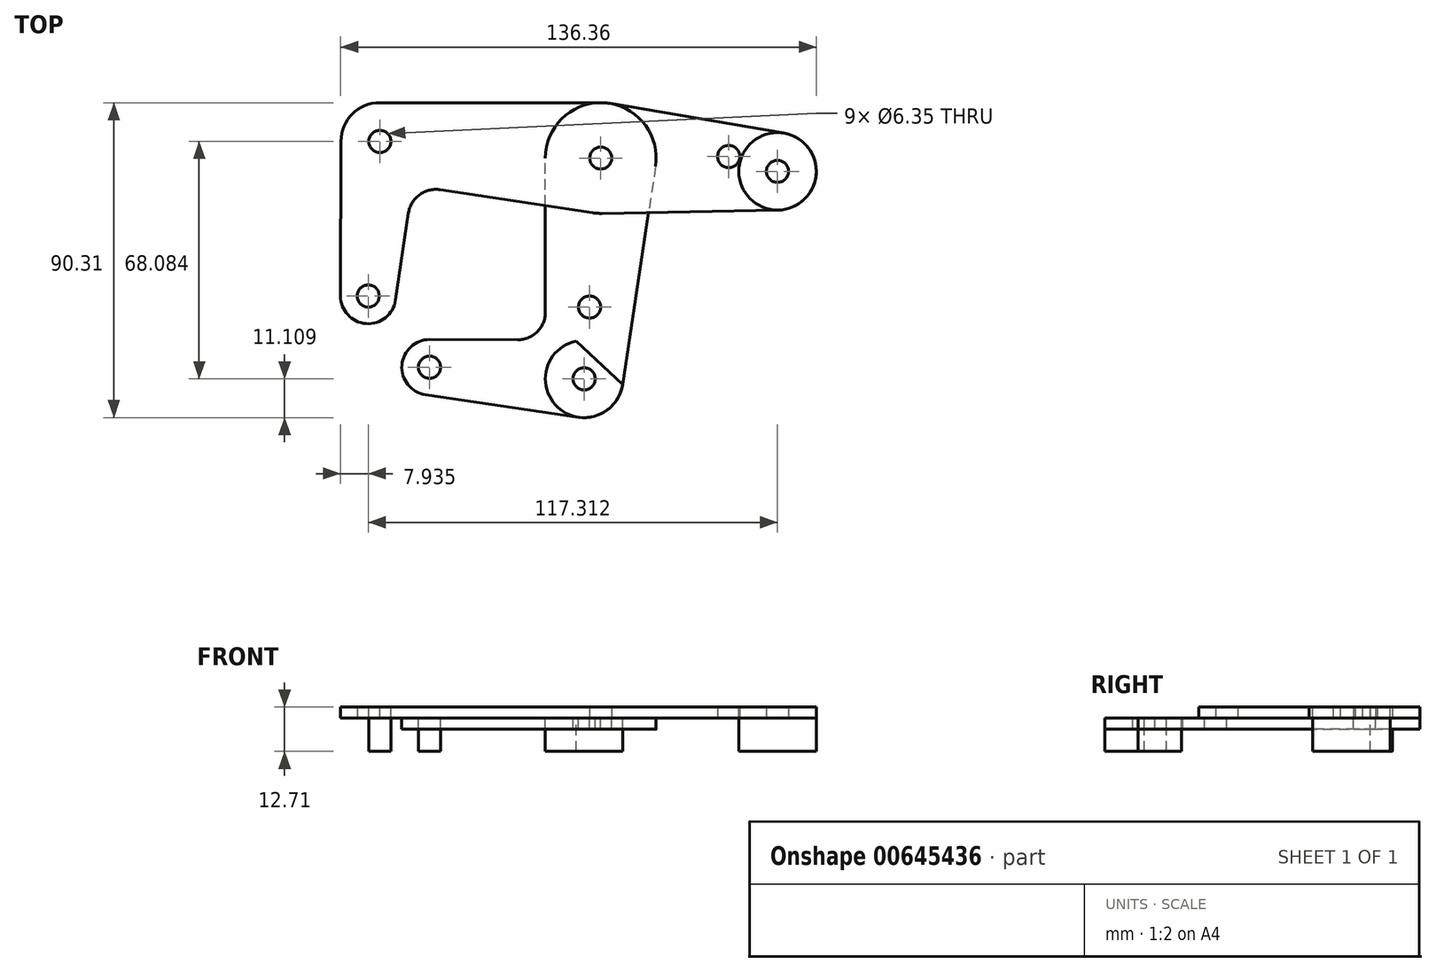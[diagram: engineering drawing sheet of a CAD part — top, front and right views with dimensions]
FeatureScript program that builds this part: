
annotation { "Feature Type Name" : "Feature", "Feature Type Description" : "" }
export const myFeature = defineFeature(function(context is Context, id is Id, definition is map)
    precondition{}
    {
        {
            var Q0;
            Q0=qCreatedBy(makeId("Top.planeOp"),FACE);
            var sketch = newSketch(context, id + "F0", { "sketchPlane" : qUnion([Q0])});
            skCircle(sketch, "E0", {"center": v(0, 0) * mm, "radius": 15.88 * mm});
            skLineSegment(sketch, "E1", {"start": v(0, 0) * mm, "end": v(-63.32, 4.76) * mm, "construction": true});
            skLineSegment(sketch, "E2", {"start": v(0, 0) * mm, "end": v(50.66, -3.8) * mm, "construction": true});
            skLineSegment(sketch, "E3", {"start": v(-63.32, 4.76) * mm, "end": v(-66.65, -39.56) * mm, "construction": true});
            skCircle(sketch, "E4", {"center": v(-63.32, 4.76) * mm, "radius": 11.11 * mm});
            skCircle(sketch, "E5", {"center": v(-66.65, -39.56) * mm, "radius": 7.94 * mm});
            skCircle(sketch, "E6", {"center": v(50.66, -3.8) * mm, "radius": 11.11 * mm});
            skCircle(sketch, "E7", {"center": v(36.66, 0.43) * mm, "radius": 3.18 * mm});
            skLineSegment(sketch, "E8", {"start": v(36.66, 0.43) * mm, "end": v(36.42, -2.74) * mm});
            skLineSegment(sketch, "E9", {"start": v(2.67, 15.65) * mm, "end": v(52.53, 7.14) * mm});
            skLineSegment(sketch, "E10", {"start": v(50.87, -14.92) * mm, "end": v(0.3, -15.87) * mm});
            skLineSegment(sketch, "E11", {"start": v(0, 0) * mm, "end": v(-4.76, -63.32) * mm, "construction": true});
            skLineSegment(sketch, "E12", {"start": v(-4.76, -63.32) * mm, "end": v(-49.09, -59.99) * mm, "construction": true});
            skCircle(sketch, "E13", {"center": v(-4.76, -63.32) * mm, "radius": 11.11 * mm});
            skLineSegment(sketch, "E14", {"start": v(-58.8, -40.72) * mm, "end": v(-55.12, -15.79) * mm});
            skLineSegment(sketch, "E15", {"start": v(-2.37, -15.7) * mm, "end": v(-46.07, -9.09) * mm});
            skArc(sketch, "E16.filletArc", {"start": v(-46.07, -9.09) * mm, "mid": v(-51.99, -10.56) * mm, "end": v(-55.12, -15.79) * mm});
            skCircle(sketch, "E17", {"center": v(-49.09, -59.99) * mm, "radius": 7.94 * mm});
            skCircle(sketch, "E18", {"center": v(-3.21, -42.73) * mm, "radius": 3.18 * mm});
            skLineSegment(sketch, "E19", {"start": v(-74.6, -39.53) * mm, "end": v(-74.43, 4.8) * mm});
            skLineSegment(sketch, "E20", {"start": v(-63.32, 15.87) * mm, "end": v(0, 15.87) * mm});
            skLineSegment(sketch, "E21", {"start": v(-15.88, -44.2) * mm, "end": v(-15.88, 0) * mm});
            skLineSegment(sketch, "E22", {"start": v(15.7, -2.37) * mm, "end": v(6.22, -64.98) * mm});
            skLineSegment(sketch, "E23", {"start": v(-6.39, -74.31) * mm, "end": v(-50.25, -67.84) * mm});
            skLineSegment(sketch, "E24", {"start": v(-23.85, -52.14) * mm, "end": v(-49.06, -52.05) * mm});
            skCircle(sketch, "E25", {"center": v(50.66, -3.8) * mm, "radius": 3.18 * mm});
            skCircle(sketch, "E26", {"center": v(0, 0) * mm, "radius": 3.18 * mm});
            skCircle(sketch, "E27", {"center": v(-63.32, 4.76) * mm, "radius": 3.18 * mm});
            skCircle(sketch, "E28", {"center": v(-66.65, -39.56) * mm, "radius": 3.18 * mm});
            skCircle(sketch, "E29", {"center": v(-49.09, -59.99) * mm, "radius": 3.18 * mm});
            skCircle(sketch, "E30", {"center": v(-4.76, -63.32) * mm, "radius": 3.18 * mm});
            skArc(sketch, "E31.filletArc", {"start": v(-23.85, -52.14) * mm, "mid": v(-18.21, -49.82) * mm, "end": v(-15.88, -44.2) * mm});
            skLineSegment(sketch, "E32", {"start": v(-66.65, -39.56) * mm, "end": v(-49.09, -59.99) * mm, "construction": true});
            skSolve(sketch);
        }
        {
            var Q0;
            {var subQ0=sQuery(id+"F0.wireOp",EDGE,"E14");Q0=makeQuery(id+"F0.imprint","IMPRINT",FACE,{"disambiguationData":[TD([[makeQuery(id+"F0.imprint","IMPRINT",EDGE,{"derivedFrom":subQ0}),1.0]])]});}
            var Q1;
            Q1=makeQuery(id+"F0.imprint","IMPRINT",FACE,{"disambiguationData":[TD([[makeQuery(id+"F0.imprint","IMPRINT",EDGE,{"derivedFrom":sQuery(id+"F0.wireOp",EDGE,"E27")}),-1.0]])]});
            var Q2;
            Q2=makeQuery(id+"F0.imprint","IMPRINT",FACE,{"disambiguationData":[TD([[makeQuery(id+"F0.imprint","IMPRINT",EDGE,{"derivedFrom":sQuery(id+"F0.wireOp",EDGE,"E26")}),-1.0]])]});
            var Q3;
            Q3=makeQuery(id+"F0.imprint","IMPRINT",FACE,{"disambiguationData":[TD([[makeQuery(id+"F0.imprint","IMPRINT",EDGE,{"derivedFrom":sQuery(id+"F0.wireOp",EDGE,"E25")}),-1.0]])]});
            var Q4;
            Q4=makeQuery(id+"F0.imprint","IMPRINT",FACE,{"disambiguationData":[TD([[makeQuery(id+"F0.imprint","IMPRINT",EDGE,{"derivedFrom":sQuery(id+"F0.wireOp",EDGE,"E7")}),-1.0]])]});
            var Q5;
            {var subQ0=sQuery(id+"F0.wireOp",EDGE,"E10");var subQ1=sQuery(id+"F0.wireOp",EDGE,"E0");var subQ2=makeQuery(id+"F0.imprint","INTERSECT",VERTEX,{"derivedFrom":[subQ1,subQ0]});Q5=makeQuery(id+"F0.imprint","IMPRINT",FACE,{"disambiguationData":[TD([[makeQuery(id+"F0.imprint","IMPRINT",EDGE,{"disambiguationData":[TD([[subQ2,-1.0]])],"derivedFrom":subQ1}),-1.0]])]});}
            var Q6;
            {var subQ0=sQuery(id+"F0.wireOp",EDGE,"E15");var subQ1=sQuery(id+"F0.wireOp",EDGE,"E0");var subQ2=makeQuery(id+"F0.imprint","INTERSECT",VERTEX,{"derivedFrom":[subQ1,subQ0]});Q6=makeQuery(id+"F0.imprint","IMPRINT",FACE,{"disambiguationData":[TD([[makeQuery(id+"F0.imprint","IMPRINT",EDGE,{"disambiguationData":[TD([[subQ2,1.0]])],"derivedFrom":subQ1}),-1.0]])]});}
            var Q7;
            Q7=makeQuery(id+"F0.imprint","IMPRINT",FACE,{"disambiguationData":[TD([[makeQuery(id+"F0.imprint","IMPRINT",EDGE,{"derivedFrom":sQuery(id+"F0.wireOp",EDGE,"E28")}),-1.0]])]});
            extrude(context, id + "F1", {"entities" : qUnion([Q0, Q1, Q2, Q3, Q4, Q5, Q6, Q7]), "depth" : 3.17 * mm, "offsetDistance" : 25.4 * mm});
        }
        {
            var Q0;
            Q0=makeQuery(id+"F0.imprint","IMPRINT",FACE,{"disambiguationData":[TD([[makeQuery(id+"F0.imprint","IMPRINT",EDGE,{"derivedFrom":sQuery(id+"F0.wireOp",EDGE,"E18")}),-1.0]])]});
            var Q1;
            Q1=makeQuery(id+"F0.imprint","IMPRINT",FACE,{"disambiguationData":[TD([[makeQuery(id+"F0.imprint","IMPRINT",EDGE,{"derivedFrom":sQuery(id+"F0.wireOp",EDGE,"E29")}),-1.0]])]});
            var Q2;
            Q2=makeQuery(id+"F0.imprint","IMPRINT",FACE,{"disambiguationData":[TD([[makeQuery(id+"F0.imprint","IMPRINT",EDGE,{"derivedFrom":sQuery(id+"F0.wireOp",EDGE,"E30")}),-1.0]])]});
            var Q3;
            Q3=makeQuery(id+"F0.imprint","IMPRINT",FACE,{"disambiguationData":[TD([[makeQuery(id+"F0.imprint","IMPRINT",EDGE,{"derivedFrom":sQuery(id+"F0.wireOp",EDGE,"E26")}),-1.0]])]});
            var Q4;
            {var subQ0=sQuery(id+"F0.wireOp",EDGE,"E10");var subQ1=sQuery(id+"F0.wireOp",EDGE,"E0");var subQ2=makeQuery(id+"F0.imprint","INTERSECT",VERTEX,{"derivedFrom":[subQ1,subQ0]});Q4=makeQuery(id+"F0.imprint","IMPRINT",FACE,{"disambiguationData":[TD([[makeQuery(id+"F0.imprint","IMPRINT",EDGE,{"disambiguationData":[TD([[subQ2,-1.0]])],"derivedFrom":subQ1}),-1.0]])]});}
            var Q5;
            {var subQ0=sQuery(id+"F0.wireOp",EDGE,"E15");var subQ1=sQuery(id+"F0.wireOp",EDGE,"E0");var subQ2=makeQuery(id+"F0.imprint","INTERSECT",VERTEX,{"derivedFrom":[subQ1,subQ0]});Q5=makeQuery(id+"F0.imprint","IMPRINT",FACE,{"disambiguationData":[TD([[makeQuery(id+"F0.imprint","IMPRINT",EDGE,{"disambiguationData":[TD([[subQ2,1.0]])],"derivedFrom":subQ1}),-1.0]])]});}
            extrude(context, id + "F2", {"entities" : qUnion([Q0, Q1, Q2, Q3, Q4, Q5]), "oppositeDirection" : true, "depth" : 3.17 * mm, "offsetDistance" : 25.4 * mm});
        }
        {
            var Q0;
            Q0=makeQuery(id+"F1.opExtrude","CAP_FACE",FACE,{"disambiguationData":[OSD([sQuery(id+"F0.wireOp",EDGE,"E0"),sQuery(id+"F0.wireOp",EDGE,"E4"),sQuery(id+"F0.wireOp",EDGE,"E5"),sQuery(id+"F0.wireOp",EDGE,"E6"),sQuery(id+"F0.wireOp",EDGE,"E7"),sQuery(id+"F0.wireOp",EDGE,"E9"),sQuery(id+"F0.wireOp",EDGE,"E10"),sQuery(id+"F0.wireOp",EDGE,"E14"),sQuery(id+"F0.wireOp",EDGE,"E15"),sQuery(id+"F0.wireOp",EDGE,"E16.filletArc"),sQuery(id+"F0.wireOp",EDGE,"E19"),sQuery(id+"F0.wireOp",EDGE,"E20"),sQuery(id+"F0.wireOp",EDGE,"E25"),sQuery(id+"F0.wireOp",EDGE,"E26"),sQuery(id+"F0.wireOp",EDGE,"E27"),sQuery(id+"F0.wireOp",EDGE,"E28")])],"isStart":false});
            var sketch = newSketch(context, id + "F3", { "sketchPlane" : qUnion([Q0])});
            skCircle(sketch, "E33", {"center": v(-63.32, 4.76) * mm, "radius": 3.98 * mm});
            skCircle(sketch, "E34", {"center": v(0, 0) * mm, "radius": 3.98 * mm});
            skCircle(sketch, "E35", {"center": v(50.66, -3.8) * mm, "radius": 11.11 * mm});
            skSolve(sketch);
        }
        {
            var Q0;
            Q0=makeQuery(id+"F2.opExtrude","CAP_FACE",FACE,{"disambiguationData":[OSD([sQuery(id+"F0.wireOp",EDGE,"E0"),sQuery(id+"F0.wireOp",EDGE,"E13"),sQuery(id+"F0.wireOp",EDGE,"E17"),sQuery(id+"F0.wireOp",EDGE,"E18"),sQuery(id+"F0.wireOp",EDGE,"E21"),sQuery(id+"F0.wireOp",EDGE,"E22"),sQuery(id+"F0.wireOp",EDGE,"E23"),sQuery(id+"F0.wireOp",EDGE,"E24"),sQuery(id+"F0.wireOp",EDGE,"E26"),sQuery(id+"F0.wireOp",EDGE,"E29"),sQuery(id+"F0.wireOp",EDGE,"E30"),sQuery(id+"F0.wireOp",EDGE,"E31.filletArc")])],"isStart":true});
            var sketch = newSketch(context, id + "F4", { "sketchPlane" : qUnion([Q0])});
            skArc(sketch, "E36.0", {"start": v(-6.39, -74.31) * mm, "mid": v(1.85, -72.25) * mm, "end": v(6.22, -64.98) * mm});
            skPoint(sketch, "E37.0", {"position": v(50.66, -3.8) * mm});
            skArc(sketch, "E38", {"start": v(6.22, -64.98) * mm, "mid": v(-11.37, -54.39) * mm, "end": v(-6.39, -74.31) * mm});
            skLineSegment(sketch, "E39", {"start": v(-7.1, -52.46) * mm, "end": v(6.24, -64.89) * mm});
            skLineSegment(sketch, "E40", {"start": v(-0.43, -58.67) * mm, "end": v(50.66, -3.8) * mm, "construction": true});
            skSolve(sketch);
        }
        {
            var Q0;
            Q0=qCreatedBy(makeId("Top.planeOp"),FACE);
            cPlane(context, id + "F5", {"entities" : qUnion([Q0]), "cplaneType" : CPlaneType.OFFSET, "offset" : 9.52 * mm, "oppositeDirection" : true, "width" : 152.4 * mm, "height" : 152.4 * mm});
        }
        {
            var Q0;
            Q0=makeQuery(id+"F4.imprint","IMPRINT",FACE,{"disambiguationData":[TD([[makeQuery(id+"F4.imprint","IMPRINT",EDGE,{"derivedFrom":makeQuery(id+"F2.opExtrude","CAP_EDGE",EDGE,{"disambiguationData":[OSD([sQuery(id+"F0.wireOp",EDGE,"E29")])],"isStart":true})}),1.0]])]});
            var Q1;
            Q1=makeQuery(id+"F3.imprint","IMPRINT",FACE,{"disambiguationData":[TD([[makeQuery(id+"F3.imprint","IMPRINT",EDGE,{"derivedFrom":makeQuery(id+"F1.opExtrude","CAP_EDGE",EDGE,{"disambiguationData":[OSD([sQuery(id+"F0.wireOp",EDGE,"E27")])],"isStart":false})}),1.0]])]});
            var Q2;
            Q2=makeQuery(id+"F3.imprint","IMPRINT",FACE,{"disambiguationData":[TD([[makeQuery(id+"F3.imprint","IMPRINT",EDGE,{"derivedFrom":makeQuery(id+"F1.opExtrude","CAP_EDGE",EDGE,{"disambiguationData":[OSD([sQuery(id+"F0.wireOp",EDGE,"E25")])],"isStart":false})}),-1.0]])]});
            var Q3;
            {var subQ2=sQuery(id+"F4.wireOp",EDGE,"E36.0");Q3=makeQuery(id+"F4.imprint","IMPRINT",FACE,{"disambiguationData":[TD([[makeQuery(id+"F4.imprint","IMPRINT",EDGE,{"derivedFrom":subQ2}),1.0]])]});}
            var Q4;
            Q4=makeQuery(id+"F3.imprint","IMPRINT",FACE,{"disambiguationData":[TD([[makeQuery(id+"F3.imprint","IMPRINT",EDGE,{"derivedFrom":makeQuery(id+"F1.opExtrude","CAP_EDGE",EDGE,{"disambiguationData":[OSD([sQuery(id+"F0.wireOp",EDGE,"E25")])],"isStart":false})}),1.0]])]});
            var Q5;
            Q5=makeQuery(id+"F4.imprint","IMPRINT",FACE,{"disambiguationData":[TD([[makeQuery(id+"F4.imprint","IMPRINT",EDGE,{"derivedFrom":makeQuery(id+"F2.opExtrude","CAP_EDGE",EDGE,{"disambiguationData":[OSD([sQuery(id+"F0.wireOp",EDGE,"E30")])],"isStart":true})}),1.0]])]});
            var Q6;
            Q6=qCreatedBy(id+"F5.planeOp",FACE);
            extrude(context, id + "F6", {"entities" : qUnion([Q0, Q1, Q2, Q3, Q4, Q5]), "endBound" : BoundingType.UP_TO_SURFACE, "oppositeDirection" : true, "depth" : 25.4 * mm, "endBoundEntityFace" : qUnion([Q6]), "offsetDistance" : 25.4 * mm});
        }
    });
